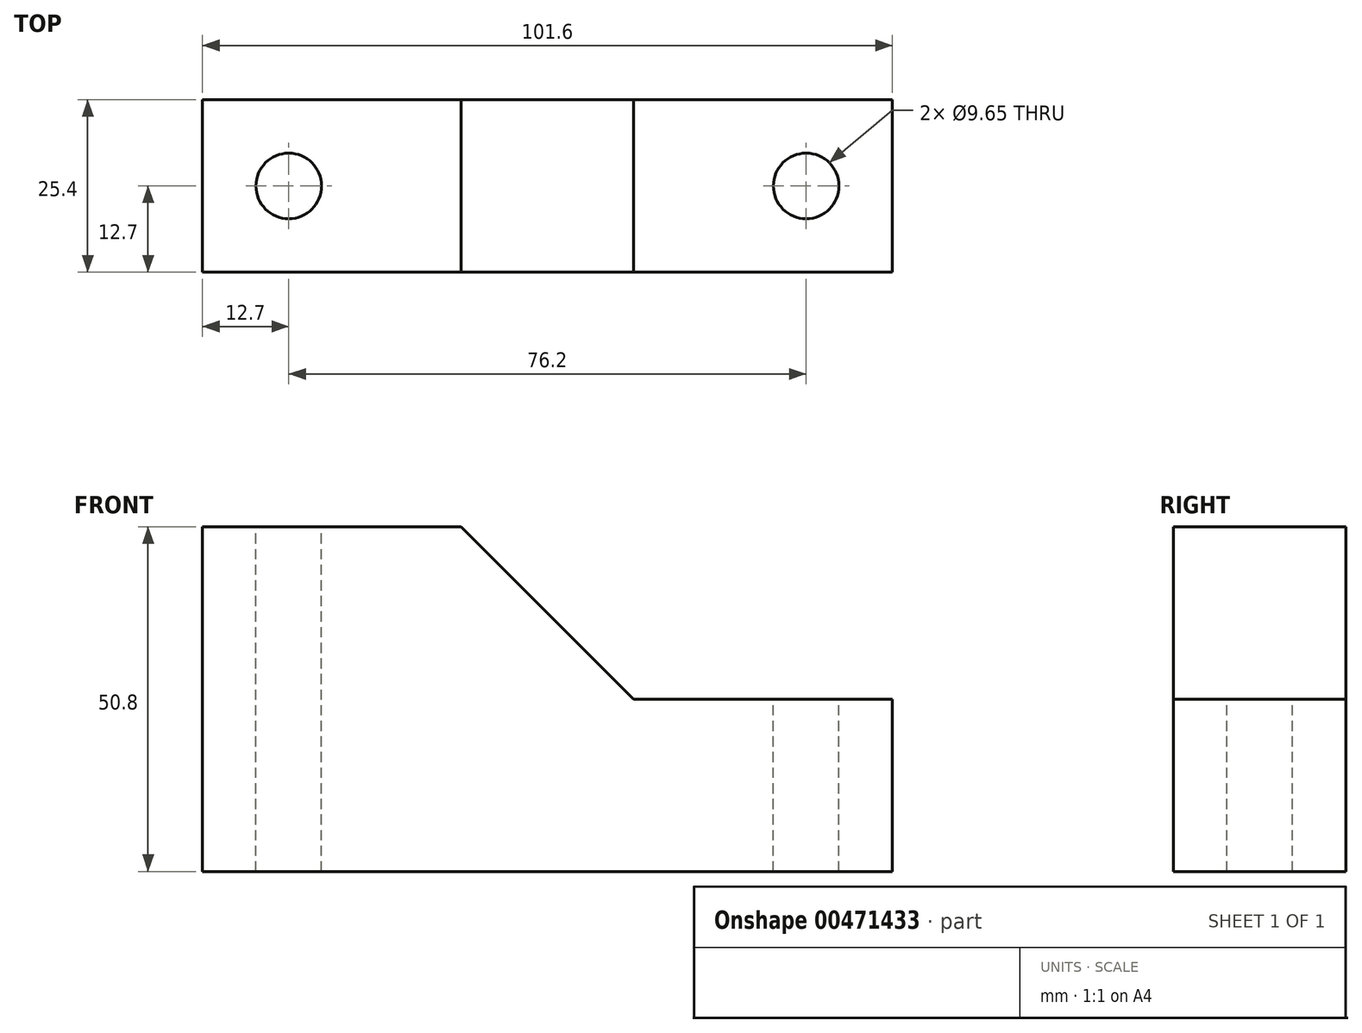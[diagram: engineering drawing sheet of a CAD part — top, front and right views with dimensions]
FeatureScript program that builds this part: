
annotation { "Feature Type Name" : "Feature", "Feature Type Description" : "" }
export const myFeature = defineFeature(function(context is Context, id is Id, definition is map)
    precondition{}
    {
        {
            var Q0;
            Q0=qCreatedBy(makeId("Front.planeOp"),FACE);
            var sketch = newSketch(context, id + "F0", { "sketchPlane" : qUnion([Q0])});
            skLineSegment(sketch, "E0", {"start": v(-101.6, 50.8) * mm, "end": v(-101.6, 0) * mm});
            skLineSegment(sketch, "E1", {"start": v(-101.6, 0) * mm, "end": v(0, 0) * mm});
            skLineSegment(sketch, "E2", {"start": v(-101.6, 50.8) * mm, "end": v(-63.5, 50.8) * mm});
            skLineSegment(sketch, "E3", {"start": v(0, 0) * mm, "end": v(0, 25.4) * mm});
            skLineSegment(sketch, "E4", {"start": v(0, 25.4) * mm, "end": v(-38.1, 25.4) * mm});
            skLineSegment(sketch, "E5", {"start": v(-38.1, 25.4) * mm, "end": v(-63.5, 50.8) * mm});
            skSolve(sketch);
        }
        {
            var Q0;
            Q0 = qSketchRegion(id + "F0", true);
            extrude(context, id + "F1", {"entities" : qUnion([Q0]), "depth" : 25.4 * mm});
        }
        {
            var Q0;
            Q0=makeQuery(id+"F1.opExtrude","SWEPT_FACE",FACE,{"disambiguationData":[OSD([sQuery(id+"F0.wireOp",EDGE,"E2")])]});
            var sketch = newSketch(context, id + "F2", { "sketchPlane" : qUnion([Q0])});
            skCircle(sketch, "E6", {"center": v(-88.9, -12.7) * mm, "radius": 4.83 * mm});
            skSolve(sketch);
        }
        {
            var Q0;
            Q0 = qSketchRegion(id + "F2", true);
            extrude(context, id + "F3", {"entities" : qUnion([Q0]), "operationType" : NewBodyOperationType.REMOVE, "endBound" : BoundingType.THROUGH_ALL, "oppositeDirection" : true, "depth" : 25.4 * mm});
        }
        {
            var Q0;
            Q0=makeQuery(id+"F1.opExtrude","SWEPT_FACE",FACE,{"disambiguationData":[OSD([sQuery(id+"F0.wireOp",EDGE,"E4")])]});
            var sketch = newSketch(context, id + "F4", { "sketchPlane" : qUnion([Q0])});
            skCircle(sketch, "E7", {"center": v(-12.7, -12.7) * mm, "radius": 4.83 * mm});
            skSolve(sketch);
        }
        {
            var Q0;
            Q0=sQuery(id+"F4.wireOp",VERTEX,"E7.center");
            var Q1;
            Q1=makeQuery(id+"F1.opExtrude","SWEPT_BODY",BODY,{"disambiguationData":[OSD([sQuery(id+"F0.wireOp",EDGE,"E0"),sQuery(id+"F0.wireOp",EDGE,"E1"),sQuery(id+"F0.wireOp",EDGE,"E2"),sQuery(id+"F0.wireOp",EDGE,"E3"),sQuery(id+"F0.wireOp",EDGE,"E4"),sQuery(id+"F0.wireOp",EDGE,"E5")])]});
            hole(context, id + "F5", {"style" : HoleStyle.SIMPLE, "endStyle" : HoleEndStyle.THROUGH, "holeDiameter" : 9.65 * mm, "isTappedThrough" : true, "tappedDepth" : 12.7 * mm, "tapClearance" : 3, "locations" : qUnion([Q0]), "scope" : qUnion([Q1])});
        }
        {
            var Q0;
            Q0=makeQuery(id+"F1.opExtrude","SWEPT_FACE",FACE,{"disambiguationData":[OSD([sQuery(id+"F0.wireOp",EDGE,"E5")])]});
            var sketch = newSketch(context, id + "F6", { "sketchPlane" : qUnion([Q0])});
            skLineSegment(sketch, "E8.bottom", {"start": v(-60.96, -7.62) * mm, "end": v(-68.58, -7.62) * mm});
            skLineSegment(sketch, "E8.top", {"start": v(-60.96, -17.78) * mm, "end": v(-68.58, -17.78) * mm});
            skLineSegment(sketch, "E8.left", {"start": v(-60.96, -7.62) * mm, "end": v(-60.96, -17.78) * mm});
            skLineSegment(sketch, "E8.right", {"start": v(-68.58, -7.62) * mm, "end": v(-68.58, -17.78) * mm});
            skPoint(sketch, "E8.middle", {"position": v(-64.77, -12.7) * mm});
            skSolve(sketch);
        }
        {
            var Q0;
            Q0=makeQuery(id+"F6.imprint","IMPRINT",FACE,{"disambiguationData":[TD([[makeQuery(id+"F6.imprint","IMPRINT",EDGE,{"derivedFrom":sQuery(id+"F6.wireOp",EDGE,"E8.bottom")}),1.0]])]});
            extrude(context, id + "F7", {"entities" : qUnion([Q0]), "operationType" : NewBodyOperationType.REMOVE, "endBound" : BoundingType.THROUGH_ALL, "oppositeDirection" : true, "depth" : 25.4 * mm});
        }
    });
